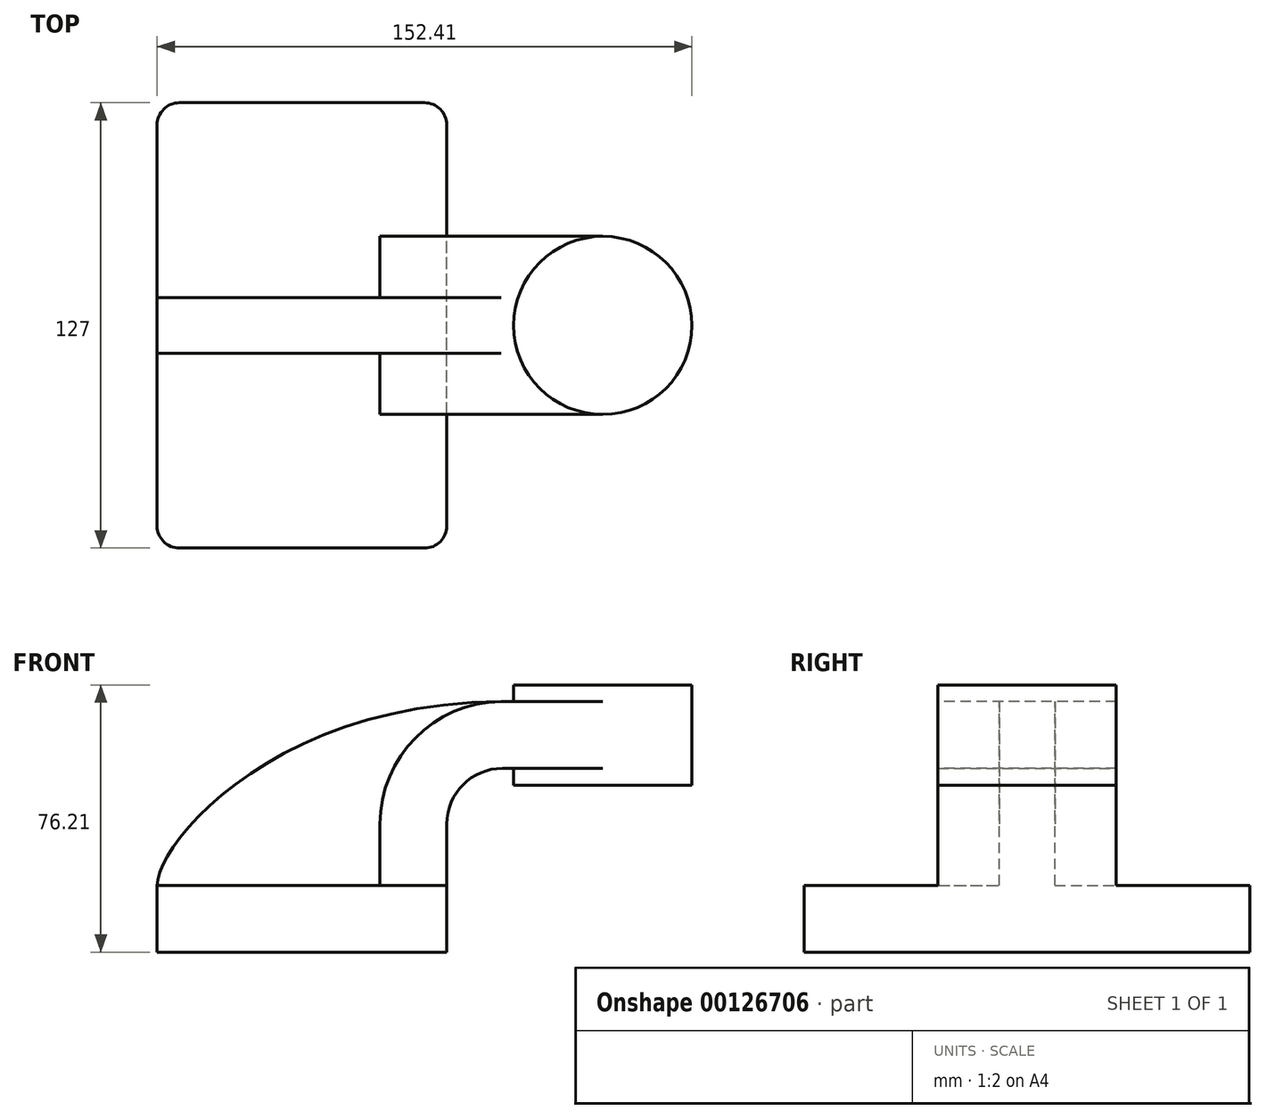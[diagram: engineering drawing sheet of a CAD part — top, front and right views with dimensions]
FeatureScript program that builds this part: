
annotation { "Feature Type Name" : "Feature", "Feature Type Description" : "" }
export const myFeature = defineFeature(function(context is Context, id is Id, definition is map)
    precondition{}
    {
        {
            var Q0;
            Q0=qCreatedBy(makeId("Front.planeOp"),FACE);
            var sketch = newSketch(context, id + "F0", { "sketchPlane" : qUnion([Q0])});
            skLineSegment(sketch, "E0.bottom", {"start": v(41.27, 9.53) * mm, "end": v(-41.28, 9.53) * mm});
            skLineSegment(sketch, "E0.top", {"start": v(41.28, -9.52) * mm, "end": v(-41.27, -9.52) * mm});
            skLineSegment(sketch, "E0.left", {"start": v(41.28, 9.53) * mm, "end": v(41.28, -9.52) * mm});
            skLineSegment(sketch, "E0.right", {"start": v(-41.28, 9.53) * mm, "end": v(-41.27, -9.52) * mm});
            skPoint(sketch, "E0.middle", {"position": v(0, 0) * mm});
            skLineSegment(sketch, "E1.bottom", {"start": v(111.12, 38.1) * mm, "end": v(60.32, 38.1) * mm});
            skLineSegment(sketch, "E1.top", {"start": v(111.12, 66.68) * mm, "end": v(60.32, 66.68) * mm});
            skLineSegment(sketch, "E1.left", {"start": v(111.12, 38.1) * mm, "end": v(111.12, 66.68) * mm});
            skLineSegment(sketch, "E1.right", {"start": v(60.32, 38.1) * mm, "end": v(60.32, 66.68) * mm});
            skPoint(sketch, "E1.middle", {"position": v(85.72, 52.39) * mm});
            skLineSegment(sketch, "E2", {"start": v(41.27, 9.53) * mm, "end": v(41.27, 27) * mm});
            skArc(sketch, "E3", {"start": v(41.27, 27) * mm, "mid": v(45.92, 38.23) * mm, "end": v(57.15, 42.88) * mm});
            skLineSegment(sketch, "E4", {"start": v(57.15, 42.88) * mm, "end": v(85.72, 42.88) * mm});
            skLineSegment(sketch, "E5.0", {"start": v(57.15, 61.93) * mm, "end": v(85.72, 61.93) * mm});
            skArc(sketch, "E5.1", {"start": v(22.23, 27) * mm, "mid": v(32.45, 51.7) * mm, "end": v(57.15, 61.93) * mm});
            skLineSegment(sketch, "E5.2", {"start": v(22.22, 9.53) * mm, "end": v(22.22, 27) * mm});
            skLineSegment(sketch, "E6", {"start": v(85.72, 66.68) * mm, "end": v(85.72, 38.1) * mm});
            skFitSpline(sketch, "E7", {"points": [v(-41.28, 9.53) * mm, v(57.15, 61.93) * mm], "startDerivative": vector(-0.17, 34.58) * mm, "endDerivative": vector(197.5, 0.9) * mm});
            skSolve(sketch);
        }
        {
            var Q0;
            Q0=makeQuery(id+"F0.imprint","IMPRINT",FACE,{"disambiguationData":[TD([[makeQuery(id+"F0.imprint","IMPRINT",EDGE,{"derivedFrom":sQuery(id+"F0.wireOp",EDGE,"E0.top")}),-1.0]])]});
            extrude(context, id + "F1", {"entities" : qUnion([Q0]), "endBound" : BoundingType.SYMMETRIC, "depth" : 127 * mm});
        }
        {
            var Q0;
            {var subQ1=sQuery(id+"F0.wireOp",EDGE,"E2");Q0=makeQuery(id+"F0.imprint","IMPRINT",FACE,{"disambiguationData":[TD([[makeQuery(id+"F0.imprint","IMPRINT",EDGE,{"derivedFrom":subQ1}),1.0]])]});}
            var Q1;
            {var subQ0=sQuery(id+"F0.wireOp",EDGE,"E4");var subQ1=sQuery(id+"F0.wireOp",EDGE,"E1.right");var subQ2=makeQuery(id+"F0.imprint","INTERSECT",VERTEX,{"derivedFrom":[subQ1,subQ0]});Q1=makeQuery(id+"F0.imprint","IMPRINT",FACE,{"disambiguationData":[TD([[makeQuery(id+"F0.imprint","IMPRINT",EDGE,{"disambiguationData":[TD([[subQ2,-1.0]])],"derivedFrom":subQ1}),-1.0]])]});}
            extrude(context, id + "F2", {"entities" : qUnion([Q0, Q1]), "operationType" : NewBodyOperationType.ADD, "endBound" : BoundingType.SYMMETRIC, "depth" : 50.8 * mm});
        }
        {
            var Q0;
            {var subQ3=sQuery(id+"F0.wireOp",EDGE,"E5.2");Q0=makeQuery(id+"F0.imprint","IMPRINT",FACE,{"disambiguationData":[TD([[makeQuery(id+"F0.imprint","IMPRINT",EDGE,{"derivedFrom":subQ3}),1.0]])]});}
            extrude(context, id + "F3", {"entities" : qUnion([Q0]), "operationType" : NewBodyOperationType.ADD, "endBound" : BoundingType.SYMMETRIC, "depth" : 15.88 * mm});
        }
        {
            var Q0;
            {var subQ0=sQuery(id+"F0.wireOp",EDGE,"E1.left");Q0=makeQuery(id+"F0.imprint","IMPRINT",FACE,{"disambiguationData":[TD([[makeQuery(id+"F0.imprint","IMPRINT",EDGE,{"derivedFrom":subQ0}),1.0]])]});}
            var Q1;
            Q1=sQuery(id+"F0.wireOp",EDGE,"E6");
            revolve(context, id + "F4", {"operationType" : NewBodyOperationType.ADD, "entities" : qUnion([Q0]), "axis" : qUnion([Q1]), "revolveType" : RevolveType.FULL});
        }
        {
            var Q0;
            Q0=makeQuery(id+"F1.opExtrude","CAP_EDGE",EDGE,{"disambiguationData":[OSD([sQuery(id+"F0.wireOp",EDGE,"E0.right")])],"isStart":false});
            var Q1;
            Q1=makeQuery(id+"F1.opExtrude","CAP_EDGE",EDGE,{"disambiguationData":[OSD([sQuery(id+"F0.wireOp",EDGE,"E0.left")])],"isStart":false});
            var Q2;
            Q2=makeQuery(id+"F1.opExtrude","CAP_EDGE",EDGE,{"disambiguationData":[OSD([sQuery(id+"F0.wireOp",EDGE,"E0.right")])],"isStart":true});
            var Q3;
            Q3=makeQuery(id+"F1.opExtrude","CAP_EDGE",EDGE,{"disambiguationData":[OSD([sQuery(id+"F0.wireOp",EDGE,"E0.left")])],"isStart":true});
            fillet(context, id + "F5", {"entities" : qUnion([Q0, Q1, Q2, Q3]), "radius" : 6.35 * mm, "tangentPropagation" : true, "allowEdgeOverflow" : false});
        }
    });
